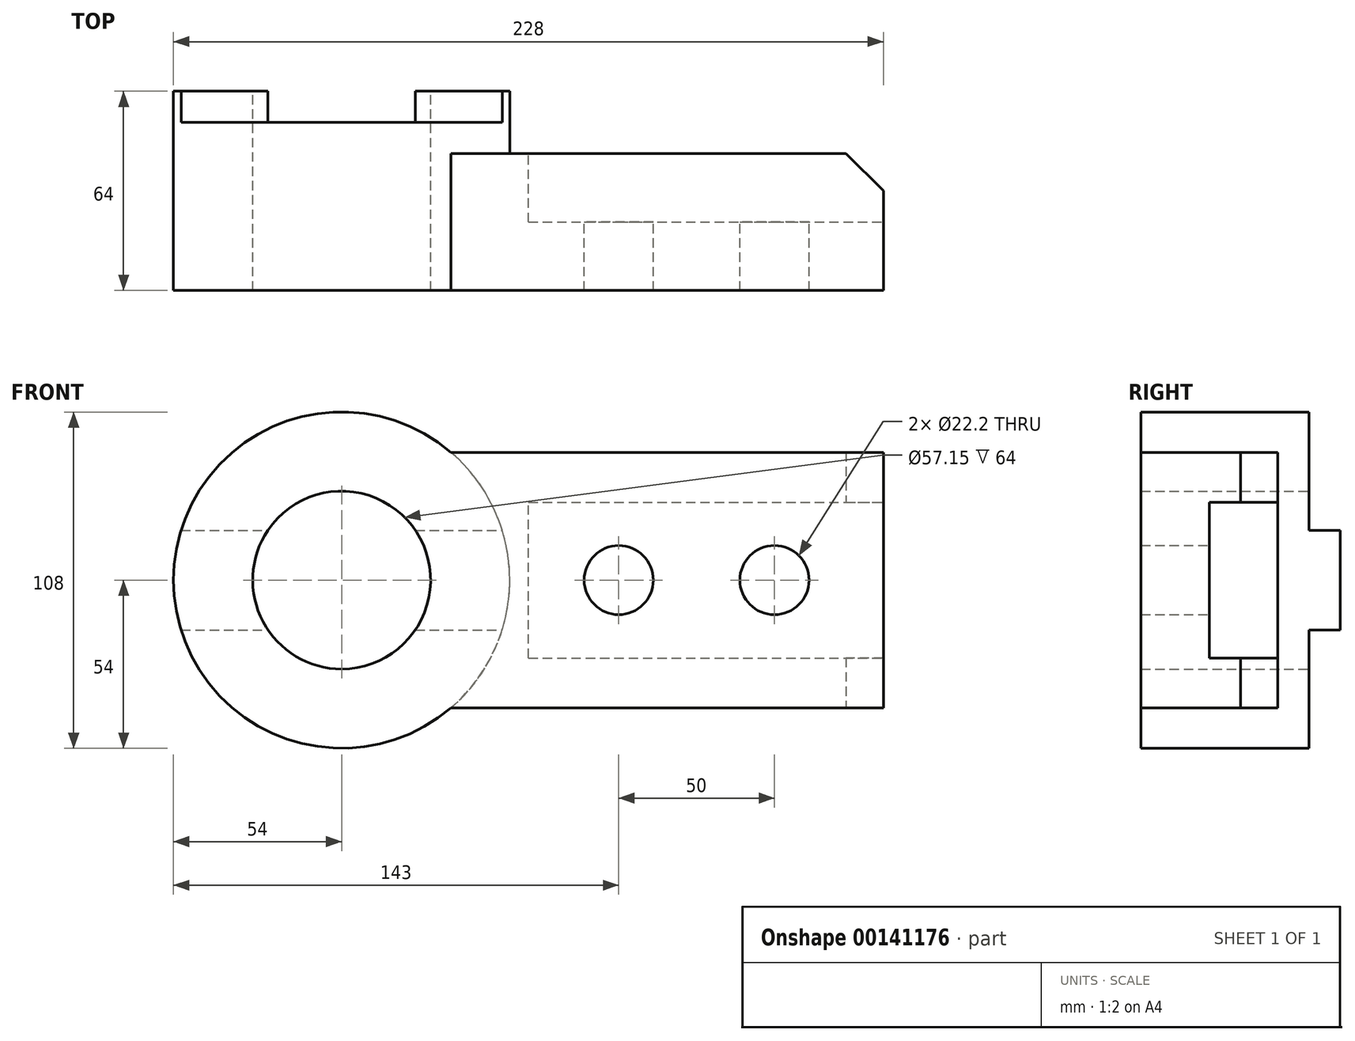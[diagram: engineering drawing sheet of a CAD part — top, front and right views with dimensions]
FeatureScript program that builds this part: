
annotation { "Feature Type Name" : "Feature", "Feature Type Description" : "" }
export const myFeature = defineFeature(function(context is Context, id is Id, definition is map)
    precondition{}
    {
        {
            var Q0;
            Q0=qCreatedBy(makeId("Front.planeOp"),FACE);
            var sketch = newSketch(context, id + "F0", { "sketchPlane" : qUnion([Q0])});
            skCircle(sketch, "E0", {"center": v(0, 0) * mm, "radius": 28.57 * mm});
            skCircle(sketch, "E1", {"center": v(0, 0) * mm, "radius": 54 * mm});
            skLineSegment(sketch, "E2", {"start": v(35.14, 41) * mm, "end": v(174, 41) * mm});
            skLineSegment(sketch, "E3", {"start": v(35.14, -41) * mm, "end": v(174, -41) * mm});
            skLineSegment(sketch, "E4", {"start": v(-51.58, 16) * mm, "end": v(51.58, 16) * mm});
            skLineSegment(sketch, "E5", {"start": v(-51.58, -16) * mm, "end": v(51.58, -16) * mm});
            skLineSegment(sketch, "E6", {"start": v(174, 41) * mm, "end": v(174, -41) * mm});
            skSolve(sketch);
        }
        {
            var Q0;
            {var subQ0=sQuery(id+"F0.wireOp",EDGE,"E4");var subQ3=sQuery(id+"F0.wireOp",EDGE,"E0");var subQ4=makeQuery(id+"F0.imprint","INTERSECT",VERTEX,{"disambiguationData":[OD(0.0)],"derivedFrom":[subQ3,subQ0]});Q0=makeQuery(id+"F0.imprint","IMPRINT",FACE,{"disambiguationData":[TD([[makeQuery(id+"F0.imprint","IMPRINT",EDGE,{"disambiguationData":[TD([[subQ4,1.0]])],"derivedFrom":subQ3}),-1.0]])]});}
            var Q1;
            {var subQ0=sQuery(id+"F0.wireOp",EDGE,"E5");var subQ3=sQuery(id+"F0.wireOp",EDGE,"E0");var subQ4=makeQuery(id+"F0.imprint","INTERSECT",VERTEX,{"disambiguationData":[OD(0.0)],"derivedFrom":[subQ3,subQ0]});Q1=makeQuery(id+"F0.imprint","IMPRINT",FACE,{"disambiguationData":[TD([[makeQuery(id+"F0.imprint","IMPRINT",EDGE,{"disambiguationData":[TD([[subQ4,-1.0]])],"derivedFrom":subQ3}),-1.0]])]});}
            var Q2;
            {var subQ0=sQuery(id+"F0.wireOp",EDGE,"E4");var subQ1=sQuery(id+"F0.wireOp",EDGE,"E0");var subQ2=makeQuery(id+"F0.imprint","INTERSECT",VERTEX,{"disambiguationData":[OD(1.0)],"derivedFrom":[subQ1,subQ0]});Q2=makeQuery(id+"F0.imprint","IMPRINT",FACE,{"disambiguationData":[TD([[makeQuery(id+"F0.imprint","IMPRINT",EDGE,{"disambiguationData":[TD([[subQ2,1.0]])],"derivedFrom":subQ1}),-1.0]])]});}
            var Q3;
            {var subQ0=sQuery(id+"F0.wireOp",EDGE,"E4");var subQ1=sQuery(id+"F0.wireOp",EDGE,"E0");var subQ2=makeQuery(id+"F0.imprint","INTERSECT",VERTEX,{"disambiguationData":[OD(0.0)],"derivedFrom":[subQ1,subQ0]});Q3=makeQuery(id+"F0.imprint","IMPRINT",FACE,{"disambiguationData":[TD([[makeQuery(id+"F0.imprint","IMPRINT",EDGE,{"disambiguationData":[TD([[subQ2,-1.0]])],"derivedFrom":subQ1}),-1.0]])]});}
            extrude(context, id + "F1", {"entities" : qUnion([Q0, Q1, Q2, Q3]), "depth" : 54 * mm});
        }
        {
            var Q0;
            {var subQ0=sQuery(id+"F0.wireOp",EDGE,"E4");var subQ1=sQuery(id+"F0.wireOp",EDGE,"E0");var subQ2=makeQuery(id+"F0.imprint","INTERSECT",VERTEX,{"disambiguationData":[OD(0.0)],"derivedFrom":[subQ1,subQ0]});Q0=makeQuery(id+"F0.imprint","IMPRINT",FACE,{"disambiguationData":[TD([[makeQuery(id+"F0.imprint","IMPRINT",EDGE,{"disambiguationData":[TD([[subQ2,-1.0]])],"derivedFrom":subQ1}),-1.0]])]});}
            var Q1;
            {var subQ0=sQuery(id+"F0.wireOp",EDGE,"E4");var subQ1=sQuery(id+"F0.wireOp",EDGE,"E0");var subQ2=makeQuery(id+"F0.imprint","INTERSECT",VERTEX,{"disambiguationData":[OD(1.0)],"derivedFrom":[subQ1,subQ0]});Q1=makeQuery(id+"F0.imprint","IMPRINT",FACE,{"disambiguationData":[TD([[makeQuery(id+"F0.imprint","IMPRINT",EDGE,{"disambiguationData":[TD([[subQ2,1.0]])],"derivedFrom":subQ1}),-1.0]])]});}
            extrude(context, id + "F2", {"entities" : qUnion([Q0, Q1]), "operationType" : NewBodyOperationType.ADD, "oppositeDirection" : true, "depth" : 10 * mm});
        }
        {
            var Q0;
            {var subQ0=sQuery(id+"F0.wireOp",EDGE,"E2");Q0=makeQuery(id+"F0.imprint","IMPRINT",FACE,{"disambiguationData":[TD([[makeQuery(id+"F0.imprint","IMPRINT",EDGE,{"derivedFrom":subQ0}),-1.0]])]});}
            extrude(context, id + "F3", {"entities" : qUnion([Q0]), "operationType" : NewBodyOperationType.ADD, "depth" : 54 * mm, "hasSecondDirection" : true, "secondDirectionOppositeDirection" : false, "secondDirectionDepth" : 10 * mm});
        }
        {
            var Q0;
            Q0=makeQuery(id+"F3.opExtrude","SWEPT_FACE",FACE,{"disambiguationData":[OSD([sQuery(id+"F0.wireOp",EDGE,"E3")])]});
            var sketch = newSketch(context, id + "F4", { "sketchPlane" : qUnion([Q0])});
            skLineSegment(sketch, "E7", {"start": v(162, 10) * mm, "end": v(174, 22) * mm});
            skLineSegment(sketch, "E8", {"start": v(174, 22) * mm, "end": v(174, 10) * mm});
            skLineSegment(sketch, "E9", {"start": v(174, 10) * mm, "end": v(162, 10) * mm});
            skSolve(sketch);
        }
        {
            var Q0;
            Q0 = qSketchRegion(id + "F4", true);
            extrude(context, id + "F5", {"entities" : qUnion([Q0]), "operationType" : NewBodyOperationType.REMOVE, "endBound" : BoundingType.THROUGH_ALL, "oppositeDirection" : true, "depth" : 25 * mm});
        }
        {
            var Q0;
            Q0=makeQuery(id+"F3.opExtrude","SWEPT_FACE",FACE,{"disambiguationData":[OSD([sQuery(id+"F0.wireOp",EDGE,"E6")])]});
            var sketch = newSketch(context, id + "F6", { "sketchPlane" : qUnion([Q0])});
            skLineSegment(sketch, "E10", {"start": v(-32, 25) * mm, "end": v(-32, -25) * mm});
            skLineSegment(sketch, "E11", {"start": v(-32, -25) * mm, "end": v(-10, -25) * mm});
            skLineSegment(sketch, "E12", {"start": v(-10, -25) * mm, "end": v(-10, 25) * mm});
            skLineSegment(sketch, "E13", {"start": v(-10, 25) * mm, "end": v(-32, 25) * mm});
            skSolve(sketch);
        }
        {
            var Q0;
            {var subQ0=sQuery(id+"F6.wireOp",EDGE,"E10");Q0=makeQuery(id+"F6.imprint","IMPRINT",FACE,{"disambiguationData":[TD([[makeQuery(id+"F6.imprint","IMPRINT",EDGE,{"derivedFrom":subQ0}),1.0]])]});}
            var Q1;
            {var subQ0=sQuery(id+"F6.wireOp",EDGE,"E12");Q1=makeQuery(id+"F6.imprint","IMPRINT",FACE,{"disambiguationData":[TD([[makeQuery(id+"F6.imprint","IMPRINT",EDGE,{"derivedFrom":subQ0}),1.0]])]});}
            extrude(context, id + "F7", {"entities" : qUnion([Q0, Q1]), "operationType" : NewBodyOperationType.REMOVE, "oppositeDirection" : true, "depth" : 114 * mm});
        }
        {
            var Q0;
            Q0=makeQuery(id+"F7.boolean.opBoolean","COPY",FACE,{"derivedFrom":makeQuery(id+"F7.opExtrude","SWEPT_FACE",FACE,{"disambiguationData":[OSD([sQuery(id+"F6.wireOp",EDGE,"E10")])]})});
            var sketch = newSketch(context, id + "F8", { "sketchPlane" : qUnion([Q0])});
            skCircle(sketch, "E14", {"center": v(-89, 0) * mm, "radius": 11.1 * mm});
            skCircle(sketch, "E15", {"center": v(-139, 0) * mm, "radius": 11.1 * mm});
            skSolve(sketch);
        }
        {
            var Q0;
            Q0=makeQuery(id+"F8.imprint","IMPRINT",FACE,{"disambiguationData":[TD([[makeQuery(id+"F8.imprint","IMPRINT",EDGE,{"derivedFrom":sQuery(id+"F8.wireOp",EDGE,"E15")}),1.0]])]});
            var Q1;
            Q1=makeQuery(id+"F8.imprint","IMPRINT",FACE,{"disambiguationData":[TD([[makeQuery(id+"F8.imprint","IMPRINT",EDGE,{"derivedFrom":sQuery(id+"F8.wireOp",EDGE,"E14")}),1.0]])]});
            extrude(context, id + "F9", {"entities" : qUnion([Q0, Q1]), "operationType" : NewBodyOperationType.REMOVE, "endBound" : BoundingType.THROUGH_ALL, "oppositeDirection" : true, "depth" : 25 * mm});
        }
    });
